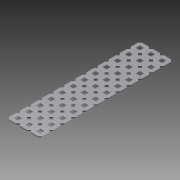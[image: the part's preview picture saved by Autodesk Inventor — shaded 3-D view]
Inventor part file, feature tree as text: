
AUTODESK INVENTOR PART (.ipt)
format: ipt  version: 2012 (Build 160160000, 160)  size: 673,280 bytes
history: native  units: in
note: dims shown in document units (in); Inventor stores cm internally (conversion verified against a paired STEP export)
features: plane x2, split x2, other x1, imported_body x1
ambient origin geometry x8: Origin, YZ Plane, XZ Plane, XY Plane, X Axis, Y Axis, Z Axis, Center Point
feature tree (6):
  parser-record x1  (decoder bookkeeping rows leaked as tree rows — omitted from the tree; the rows remain in map.json)
  imported_body  "Base1"
  plane  "Work Plane2"
  split  "Split2"
  plane  "Work Plane3"
  split  "Split3"
